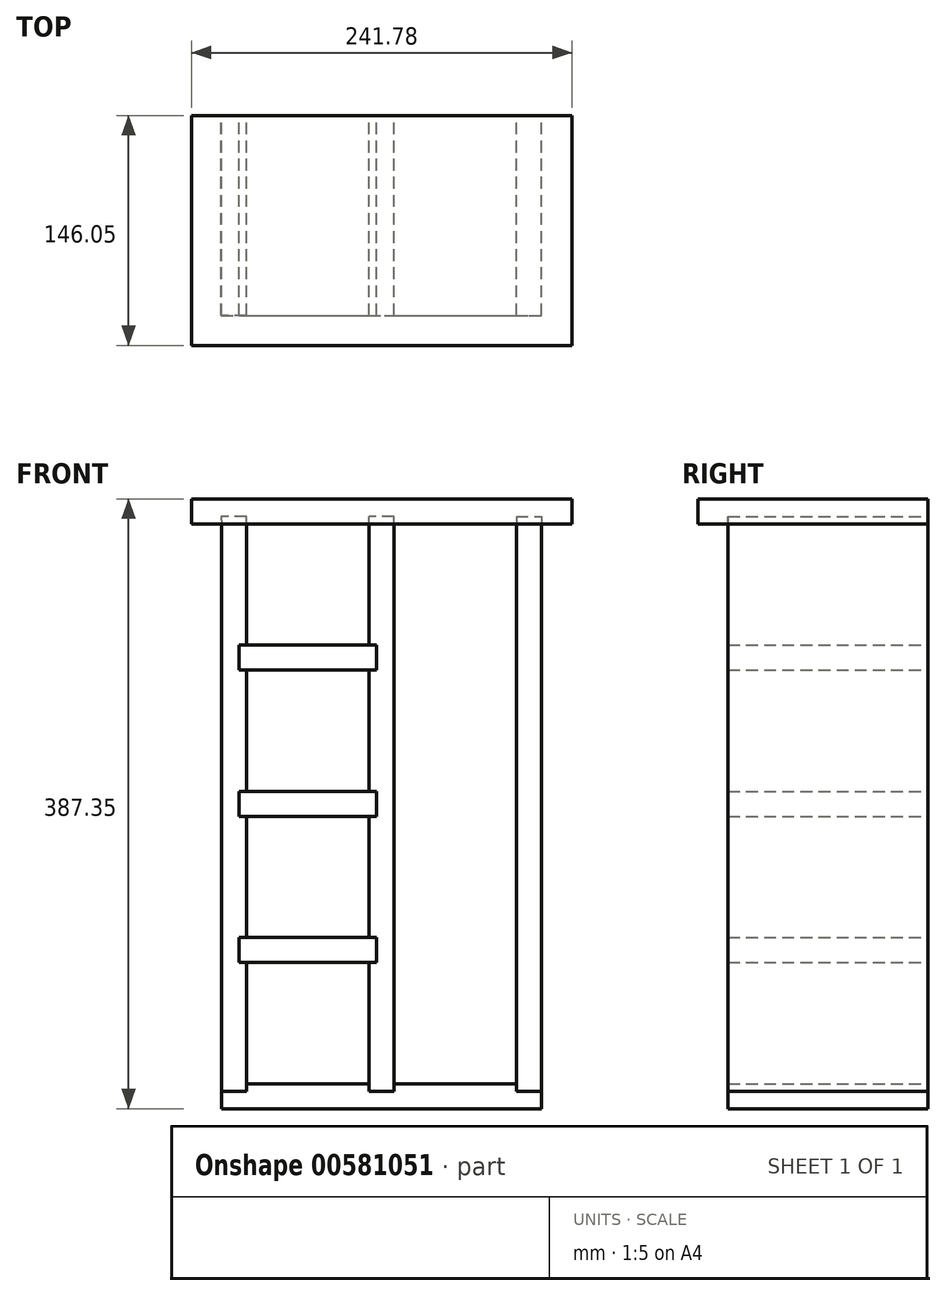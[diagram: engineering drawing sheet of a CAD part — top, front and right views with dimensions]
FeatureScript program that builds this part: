
annotation { "Feature Type Name" : "Feature", "Feature Type Description" : "" }
export const myFeature = defineFeature(function(context is Context, id is Id, definition is map)
    precondition{}
    {
        {
            var Q0;
            Q0=qCreatedBy(makeId("Front.planeOp"),FACE);
            var sketch = newSketch(context, id + "F0", { "sketchPlane" : qUnion([Q0])});
            skLineSegment(sketch, "E0.bottom", {"start": v(-58.9, 228.4) * mm, "end": v(-43.02, 228.4) * mm});
            skLineSegment(sketch, "E0.left", {"start": v(-58.9, 228.4) * mm, "end": v(-58.9, -127.2) * mm});
            skLineSegment(sketch, "E0.right", {"start": v(-43.02, 228.4) * mm, "end": v(-43.02, 151.4) * mm});
            skLineSegment(sketch, "E1.bottom", {"start": v(-43.02, -127.2) * mm, "end": v(34.77, -127.2) * mm});
            skLineSegment(sketch, "E1.top", {"start": v(-58.9, -143.08) * mm, "end": v(144.3, -143.08) * mm});
            skLineSegment(sketch, "E1.left", {"start": v(-58.9, -127.2) * mm, "end": v(-58.9, -143.08) * mm});
            skLineSegment(sketch, "E1.right", {"start": v(144.3, -127.2) * mm, "end": v(144.3, -143.08) * mm});
            skLineSegment(sketch, "E2.top", {"start": v(34.77, 228.4) * mm, "end": v(50.65, 228.4) * mm});
            skLineSegment(sketch, "E2.left", {"start": v(34.77, -127.2) * mm, "end": v(34.77, -50.22) * mm});
            skLineSegment(sketch, "E2.right", {"start": v(50.65, -127.2) * mm, "end": v(50.65, 228.4) * mm});
            skLineSegment(sketch, "E3.bottom", {"start": v(128.43, 228.4) * mm, "end": v(144.3, 228.4) * mm});
            skLineSegment(sketch, "E3.left", {"start": v(128.43, 228.4) * mm, "end": v(128.43, -127.2) * mm});
            skLineSegment(sketch, "E3.right", {"start": v(144.3, 228.4) * mm, "end": v(144.3, -127.2) * mm});
            skLineSegment(sketch, "E4", {"start": v(-43.02, -127.2) * mm, "end": v(-43.02, -131.97) * mm});
            skLineSegment(sketch, "E5", {"start": v(-43.02, -131.97) * mm, "end": v(-58.9, -131.97) * mm});
            skLineSegment(sketch, "E6", {"start": v(-58.9, -131.97) * mm, "end": v(-58.9, -127.2) * mm});
            skLineSegment(sketch, "E7", {"start": v(34.77, -127.2) * mm, "end": v(34.77, -131.97) * mm});
            skLineSegment(sketch, "E8", {"start": v(34.77, -131.97) * mm, "end": v(50.65, -131.97) * mm});
            skLineSegment(sketch, "E9", {"start": v(50.65, -131.97) * mm, "end": v(50.65, -127.2) * mm});
            skLineSegment(sketch, "E10.trimOffspring", {"start": v(50.65, -127.2) * mm, "end": v(128.43, -127.2) * mm});
            skLineSegment(sketch, "E11", {"start": v(128.43, -127.2) * mm, "end": v(128.43, -131.97) * mm});
            skLineSegment(sketch, "E12", {"start": v(128.43, -131.97) * mm, "end": v(144.3, -131.97) * mm});
            skLineSegment(sketch, "E13", {"start": v(144.3, -131.97) * mm, "end": v(144.3, -127.2) * mm});
            skLineSegment(sketch, "E14", {"start": v(34.77, 151.4) * mm, "end": v(39.53, 151.4) * mm});
            skLineSegment(sketch, "E15", {"start": v(39.53, 151.4) * mm, "end": v(39.53, 135.52) * mm});
            skLineSegment(sketch, "E16", {"start": v(39.53, 135.52) * mm, "end": v(34.77, 135.52) * mm});
            skLineSegment(sketch, "E17", {"start": v(-47.78, 135.52) * mm, "end": v(-47.78, 151.4) * mm});
            skLineSegment(sketch, "E18", {"start": v(-47.78, 151.4) * mm, "end": v(-43.02, 151.4) * mm});
            skLineSegment(sketch, "E19.trimOffspring", {"start": v(-43.02, 135.52) * mm, "end": v(-43.02, 58.53) * mm});
            skLineSegment(sketch, "E20.trimOffspring", {"start": v(34.77, 151.4) * mm, "end": v(34.77, 228.4) * mm});
            skLineSegment(sketch, "E21.trimOffspring", {"start": v(-43.02, 135.52) * mm, "end": v(-47.78, 135.52) * mm});
            skLineSegment(sketch, "E22", {"start": v(-43.02, 58.53) * mm, "end": v(-47.78, 58.53) * mm});
            skLineSegment(sketch, "E23", {"start": v(-47.78, 58.53) * mm, "end": v(-47.78, 42.65) * mm});
            skLineSegment(sketch, "E24", {"start": v(-47.78, 42.65) * mm, "end": v(-43.02, 42.65) * mm});
            skLineSegment(sketch, "E25", {"start": v(39.53, 42.65) * mm, "end": v(39.53, 58.53) * mm});
            skLineSegment(sketch, "E26", {"start": v(39.53, 58.53) * mm, "end": v(34.77, 58.53) * mm});
            skLineSegment(sketch, "E27.trimOffspring", {"start": v(34.77, 58.53) * mm, "end": v(34.77, 135.52) * mm});
            skLineSegment(sketch, "E28.trimOffspring", {"start": v(34.77, 42.65) * mm, "end": v(39.53, 42.65) * mm});
            skLineSegment(sketch, "E29.trimOffspring", {"start": v(-43.02, 42.65) * mm, "end": v(-43.02, -34.34) * mm});
            skLineSegment(sketch, "E30", {"start": v(-47.78, -34.34) * mm, "end": v(-47.78, -50.22) * mm});
            skLineSegment(sketch, "E31", {"start": v(-47.78, -50.22) * mm, "end": v(-43.02, -50.22) * mm});
            skLineSegment(sketch, "E32", {"start": v(39.53, -50.22) * mm, "end": v(39.53, -34.34) * mm});
            skLineSegment(sketch, "E33", {"start": v(39.53, -34.34) * mm, "end": v(34.77, -34.34) * mm});
            skLineSegment(sketch, "E34.trimOffspring", {"start": v(-43.02, -34.34) * mm, "end": v(-47.78, -34.34) * mm});
            skLineSegment(sketch, "E35.trimOffspring", {"start": v(34.77, -34.34) * mm, "end": v(34.77, 42.65) * mm});
            skLineSegment(sketch, "E36.trimOffspring", {"start": v(34.77, -50.22) * mm, "end": v(39.53, -50.22) * mm});
            skLineSegment(sketch, "E37.trimOffspring", {"start": v(-43.02, -50.22) * mm, "end": v(-43.02, -127.2) * mm});
            skLineSegment(sketch, "E38", {"start": v(128.43, 228.4) * mm, "end": v(128.43, 233.15) * mm});
            skLineSegment(sketch, "E39", {"start": v(128.43, 233.15) * mm, "end": v(144.3, 233.15) * mm});
            skLineSegment(sketch, "E40", {"start": v(144.3, 233.15) * mm, "end": v(144.3, 228.4) * mm});
            skLineSegment(sketch, "E41", {"start": v(50.65, 233.15) * mm, "end": v(50.65, 228.4) * mm});
            skLineSegment(sketch, "E42", {"start": v(50.65, 233.15) * mm, "end": v(34.77, 233.15) * mm});
            skPoint(sketch, "E42.endSnap0", {"position": v(34.77, 189.9) * mm});
            skLineSegment(sketch, "E43", {"start": v(34.77, 233.15) * mm, "end": v(34.77, 228.4) * mm});
            skLineSegment(sketch, "E44", {"start": v(-43.02, 228.4) * mm, "end": v(-43.02, 233.15) * mm});
            skLineSegment(sketch, "E45", {"start": v(-43.02, 233.15) * mm, "end": v(-58.95, 233.15) * mm});
            skLineSegment(sketch, "E46", {"start": v(-58.95, 233.15) * mm, "end": v(-58.9, 228.4) * mm});
            skSolve(sketch);
        }
        {
            var Q0;
            Q0=makeQuery(id+"F0.imprint","IMPRINT",FACE,{"disambiguationData":[TD([[makeQuery(id+"F0.imprint","IMPRINT",EDGE,{"derivedFrom":sQuery(id+"F0.wireOp",EDGE,"E0.bottom")}),-1.0]])]});
            var Q1;
            Q1=makeQuery(id+"F0.imprint","IMPRINT",FACE,{"disambiguationData":[TD([[makeQuery(id+"F0.imprint","IMPRINT",EDGE,{"derivedFrom":sQuery(id+"F0.wireOp",EDGE,"E2.top")}),-1.0]])]});
            var Q2;
            Q2=makeQuery(id+"F0.imprint","IMPRINT",FACE,{"disambiguationData":[TD([[makeQuery(id+"F0.imprint","IMPRINT",EDGE,{"derivedFrom":sQuery(id+"F0.wireOp",EDGE,"E3.bottom")}),-1.0]])]});
            var Q3;
            Q3=makeQuery(id+"F0.imprint","IMPRINT",FACE,{"disambiguationData":[TD([[makeQuery(id+"F0.imprint","IMPRINT",EDGE,{"derivedFrom":sQuery(id+"F0.wireOp",EDGE,"E0.bottom")}),1.0]])]});
            var Q4;
            Q4=makeQuery(id+"F0.imprint","IMPRINT",FACE,{"disambiguationData":[TD([[makeQuery(id+"F0.imprint","IMPRINT",EDGE,{"derivedFrom":sQuery(id+"F0.wireOp",EDGE,"E2.top")}),1.0]])]});
            var Q5;
            Q5=makeQuery(id+"F0.imprint","IMPRINT",FACE,{"disambiguationData":[TD([[makeQuery(id+"F0.imprint","IMPRINT",EDGE,{"derivedFrom":sQuery(id+"F0.wireOp",EDGE,"E3.bottom")}),1.0]])]});
            extrude(context, id + "F1", {"entities" : qUnion([Q0, Q1, Q2, Q3, Q4, Q5]), "depth" : 127 * mm, "offsetDistance" : 25.4 * mm});
        }
        {
            var Q0;
            Q0=makeQuery(id+"F0.imprint","IMPRINT",FACE,{"disambiguationData":[TD([[makeQuery(id+"F0.imprint","IMPRINT",EDGE,{"derivedFrom":sQuery(id+"F0.wireOp",EDGE,"E1.bottom")}),-1.0]])]});
            extrude(context, id + "F2", {"entities" : qUnion([Q0]), "depth" : 127 * mm, "offsetDistance" : 25.4 * mm});
        }
        {
            var Q0;
            Q0=qCreatedBy(makeId("Front.planeOp"),FACE);
            var sketch = newSketch(context, id + "F3", { "sketchPlane" : qUnion([Q0])});
            skLineSegment(sketch, "E47.bottom", {"start": v(-47.78, 151.4) * mm, "end": v(39.53, 151.4) * mm});
            skLineSegment(sketch, "E47.top", {"start": v(-47.78, 135.52) * mm, "end": v(39.53, 135.52) * mm});
            skLineSegment(sketch, "E47.left", {"start": v(-47.78, 151.4) * mm, "end": v(-47.78, 135.52) * mm});
            skLineSegment(sketch, "E47.right", {"start": v(39.53, 151.4) * mm, "end": v(39.53, 135.52) * mm});
            skLineSegment(sketch, "E48.bottom", {"start": v(-47.78, 58.53) * mm, "end": v(39.53, 58.53) * mm});
            skLineSegment(sketch, "E48.top", {"start": v(-47.78, 42.65) * mm, "end": v(39.53, 42.65) * mm});
            skLineSegment(sketch, "E48.left", {"start": v(-47.78, 58.53) * mm, "end": v(-47.78, 42.65) * mm});
            skLineSegment(sketch, "E48.right", {"start": v(39.53, 58.53) * mm, "end": v(39.53, 42.65) * mm});
            skLineSegment(sketch, "E49.bottom", {"start": v(-47.78, -34.34) * mm, "end": v(39.53, -34.34) * mm});
            skLineSegment(sketch, "E49.top", {"start": v(-47.78, -50.22) * mm, "end": v(39.53, -50.22) * mm});
            skLineSegment(sketch, "E49.left", {"start": v(-47.78, -34.34) * mm, "end": v(-47.78, -50.22) * mm});
            skLineSegment(sketch, "E49.right", {"start": v(39.53, -34.34) * mm, "end": v(39.53, -50.22) * mm});
            skSolve(sketch);
        }
        {
            var Q0;
            Q0 = qSketchRegion(id + "F3", true);
            extrude(context, id + "F4", {"entities" : qUnion([Q0]), "depth" : 127 * mm, "offsetDistance" : 25.4 * mm});
        }
        {
            var Q0;
            Q0=makeQuery(id+"F0.imprint","IMPRINT",FACE,{"disambiguationData":[TD([[makeQuery(id+"F0.imprint","IMPRINT",EDGE,{"derivedFrom":sQuery(id+"F0.wireOp",EDGE,"E2.top")}),-1.0]])]});
            var sketch = newSketch(context, id + "F5", { "sketchPlane" : qUnion([Q0])});
            skLineSegment(sketch, "E50", {"start": v(144.79, 228.4) * mm, "end": v(163.84, 228.4) * mm});
            skLineSegment(sketch, "E51", {"start": v(163.84, 228.4) * mm, "end": v(163.84, 244.27) * mm});
            skLineSegment(sketch, "E52", {"start": v(163.84, 244.27) * mm, "end": v(-77.94, 244.27) * mm});
            skLineSegment(sketch, "E53", {"start": v(-77.94, 244.27) * mm, "end": v(-77.94, 228.4) * mm});
            skLineSegment(sketch, "E54", {"start": v(-77.94, 228.4) * mm, "end": v(-58.9, 228.4) * mm});
            skLineSegment(sketch, "E55", {"start": v(-58.9, 228.4) * mm, "end": v(144.79, 228.4) * mm});
            skSolve(sketch);
        }
        {
            var Q0;
            Q0 = qSketchRegion(id + "F5", true);
            extrude(context, id + "F6", {"entities" : qUnion([Q0]), "depth" : 146.05 * mm, "offsetDistance" : 25.4 * mm});
        }
        {
            var Q0;
            Q0=makeQuery(id+"F1.opExtrude","SWEPT_BODY",BODY,{"disambiguationData":[OSD([sQuery(id+"F0.wireOp",EDGE,"E0.left"),sQuery(id+"F0.wireOp",EDGE,"E0.right"),sQuery(id+"F0.wireOp",EDGE,"E4"),sQuery(id+"F0.wireOp",EDGE,"E5"),sQuery(id+"F0.wireOp",EDGE,"E6"),sQuery(id+"F0.wireOp",EDGE,"E17"),sQuery(id+"F0.wireOp",EDGE,"E18"),sQuery(id+"F0.wireOp",EDGE,"E19.trimOffspring"),sQuery(id+"F0.wireOp",EDGE,"E21.trimOffspring"),sQuery(id+"F0.wireOp",EDGE,"E22"),sQuery(id+"F0.wireOp",EDGE,"E23"),sQuery(id+"F0.wireOp",EDGE,"E24"),sQuery(id+"F0.wireOp",EDGE,"E29.trimOffspring"),sQuery(id+"F0.wireOp",EDGE,"E30"),sQuery(id+"F0.wireOp",EDGE,"E31"),sQuery(id+"F0.wireOp",EDGE,"E34.trimOffspring"),sQuery(id+"F0.wireOp",EDGE,"E37.trimOffspring"),sQuery(id+"F0.wireOp",EDGE,"E44"),sQuery(id+"F0.wireOp",EDGE,"E45"),sQuery(id+"F0.wireOp",EDGE,"E46")])]});
            var Q1;
            Q1=makeQuery(id+"F1.opExtrude","SWEPT_BODY",BODY,{"disambiguationData":[OSD([sQuery(id+"F0.wireOp",EDGE,"E2.left"),sQuery(id+"F0.wireOp",EDGE,"E2.right"),sQuery(id+"F0.wireOp",EDGE,"E7"),sQuery(id+"F0.wireOp",EDGE,"E8"),sQuery(id+"F0.wireOp",EDGE,"E9"),sQuery(id+"F0.wireOp",EDGE,"E14"),sQuery(id+"F0.wireOp",EDGE,"E15"),sQuery(id+"F0.wireOp",EDGE,"E16"),sQuery(id+"F0.wireOp",EDGE,"E20.trimOffspring"),sQuery(id+"F0.wireOp",EDGE,"E25"),sQuery(id+"F0.wireOp",EDGE,"E26"),sQuery(id+"F0.wireOp",EDGE,"E27.trimOffspring"),sQuery(id+"F0.wireOp",EDGE,"E28.trimOffspring"),sQuery(id+"F0.wireOp",EDGE,"E32"),sQuery(id+"F0.wireOp",EDGE,"E33"),sQuery(id+"F0.wireOp",EDGE,"E35.trimOffspring"),sQuery(id+"F0.wireOp",EDGE,"E36.trimOffspring"),sQuery(id+"F0.wireOp",EDGE,"E41"),sQuery(id+"F0.wireOp",EDGE,"E42"),sQuery(id+"F0.wireOp",EDGE,"E43")])]});
            var Q2;
            Q2=makeQuery(id+"F1.opExtrude","SWEPT_BODY",BODY,{"disambiguationData":[OSD([sQuery(id+"F0.wireOp",EDGE,"E3.left"),sQuery(id+"F0.wireOp",EDGE,"E3.right"),sQuery(id+"F0.wireOp",EDGE,"E11"),sQuery(id+"F0.wireOp",EDGE,"E12"),sQuery(id+"F0.wireOp",EDGE,"E13"),sQuery(id+"F0.wireOp",EDGE,"E38"),sQuery(id+"F0.wireOp",EDGE,"E39"),sQuery(id+"F0.wireOp",EDGE,"E40")])]});
            var Q3;
            Q3=makeQuery(id+"F6.opExtrude","SWEPT_BODY",BODY,{"disambiguationData":[OSD([sQuery(id+"F5.wireOp",EDGE,"E50"),sQuery(id+"F5.wireOp",EDGE,"E51"),sQuery(id+"F5.wireOp",EDGE,"E52"),sQuery(id+"F5.wireOp",EDGE,"E53"),sQuery(id+"F5.wireOp",EDGE,"E54"),sQuery(id+"F5.wireOp",EDGE,"E55")])]});
            booleanBodies(context, id + "F7", {"operationType" : BooleanOperationType.SUBTRACTION, "tools" : qUnion([Q0, Q1, Q2]), "targets" : qUnion([Q3]), "keepTools" : true});
        }
    });
